# Revit family: GR_Щелевой диффузор угловой стеновой внешний с адаптером_PV_Вытяжка_R21
name_source: partatom
category: Воздухораспределители
units: mm (PartAtom-declared; Revit-internal decimal feet)

## family parameters
Всегда вертикально = Да
Заголовок OmniClass = Diffusers, Registers, and Grilles
На основе рабочей плоскости = Нет
Номер OmniClass = 23.75.70.21.27.11
Общий = Нет
При загрузке вырезать с полостями = Да
Размер круглого соединителя = Использовать диаметр
Тип детали = Нормальный
Точка принадлежности помещению = Нет

## types (15) — shared parameters
ADSK_URL страницы изделия = https://grilles.ru
ADSK_Автор = THE GRILLES
ADSK_Версия Revit = 2021
ADSK_Единица измерения = шт.
ADSK_Завод-изготовитель = ООО "ВЕНТРЕШЕТКИКОМ"
ADSK_Количество = 1
GR_Материал дефлекторов = Алюминий, RAL 9005M, черный
GR_Материал корпуса = Алюминий, RAL 9016M, белый
URL = https://grilles.ru
ДФ_Без_Имя = Щелевой диффузор угловой стеновой внутренний серии PV без дефлектора
ДФ_Рег_Имя = Щелевой диффузор угловой стеновой внутренний серии PV c регулируемым дефлектором
ДФ_Фикс_Имя = Щелевой диффузор угловой стеновой внутренний серии PV c фиксированным дефлектором
Заглушка_Толщина = 1 мм
Изготовитель = ООО "ВЕНТРЕШЕТКИКОМ"
Макс.Длина = 450 мм
Мин.Длина = 200 мм
Основа_Высота = 10 мм
Ширина_Боковой_Ламели = 28.5 мм
Ширина_Центральной_Ламели = 27 мм
zero-valued in all types: Отметка по умолчанию

## per-type parameters (varying)
| type | ADSK_Размер_Ширина | ДФ_Ширина(По каталогу) | Количество_Щелей(По каталогу) | Корпус_Высота | Корпус_Ширина | Муфта_Длина | Общая_Ширина_Щелей(По каталогу) | Расстояние между ламелями(Деф) | Расстояние между ламелями(Кронштейн) | Щель_Ширина(По каталогу) |
| PV 1-20-U3 | 48 мм | 27 мм | 1 | 182 мм | 90 мм | 47 мм | 20 мм | 45.5 мм | 45.5 мм | 20 мм |
| PV 1-30-U3 | 58 мм | 32 мм | 1 | 182 мм | 95 мм | 50 мм | 30 мм | 55.5 мм | 55.5 мм | 30 мм |
| PV 1-40-U3 | 68 мм | 40 мм | 1 | 222 мм | 100 мм | 50 мм | 40 мм | 65.5 мм | 65.5 мм | 40 мм |
| PV 1-50-U3 | 78 мм | 50 мм | 1 | 222 мм | 105 мм | 50 мм | 50 мм | 75.5 мм | 75.5 мм | 50 мм |
| PV 1-60-U3 | 88 мм | 65 мм | 1 | 272 мм | 110 мм | 50 мм | 60 мм | 85.5 мм | 85.5 мм | 60 мм |
| PV 1-70-U3 | 98 мм | 75 мм | 1 | 272 мм | 115 мм | 50 мм | 70 мм | 95.5 мм | 95.5 мм | 70 мм |
| PV 2-20-U3 | 95 мм | 27 мм | 2 | 222 мм | 135 мм | 50 мм | 67 мм | 45.5 мм | 45.5 мм | 20 мм |
| PV 2-25-U3 | 105 мм | 27.5 мм | 2 | 222 мм | 145 мм | 50 мм | 77 мм | 50.5 мм | 50.5 мм | 25 мм |
| PV 2-30-U3 | 115 мм | 32 мм | 2 | 222 мм | 155 мм | 50 мм | 87 мм | 55.5 мм | 55.5 мм | 30 мм |
| PV 3-20-U3 | 142 мм | 27 мм | 3 | 222 мм | 185 мм | 50 мм | 114 мм | 45.5 мм | 45.5 мм | 20 мм |
| PV 3-25-U3 | 157 мм | 27.5 мм | 3 | 222 мм | 200 мм | 50 мм | 129 мм | 50.5 мм | 50.5 мм | 25 мм |
| PV 3-30-U3 | 172 мм | 32 мм | 3 | 222 мм | 215 мм | 50 мм | 144 мм | 55.5 мм | 55.5 мм | 30 мм |
| PV 4-20-U3 | 189 мм | 27 мм | 4 | 272 мм | 230 мм | 50 мм | 161 мм | 45.5 мм | 45.5 мм | 20 мм |
| PV 4-25-U3 | 209 мм | 27.5 мм | 4 | 272 мм | 250 мм | 50 мм | 181 мм | 50.5 мм | 50.5 мм | 25 мм |
| PV 4-30-U3 | 229 мм | 32 мм | 4 | 272 мм | 270 мм | 50 мм | 201 мм | 55.5 мм | 55.5 мм | 30 мм |

note: column(s) folded — value = type name in every type: ADSK_Марка
